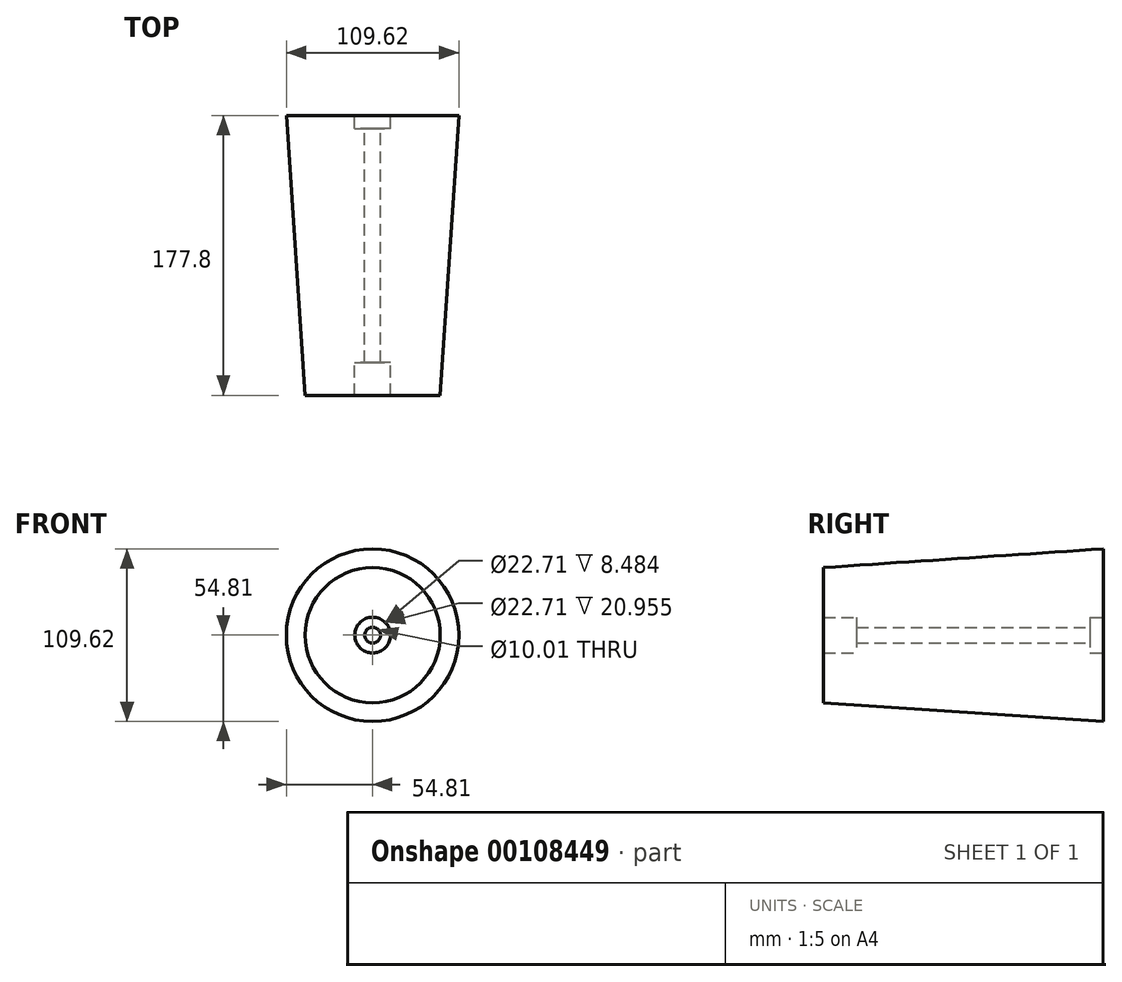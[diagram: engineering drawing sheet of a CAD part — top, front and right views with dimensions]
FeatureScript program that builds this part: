
annotation { "Feature Type Name" : "Feature", "Feature Type Description" : "" }
export const myFeature = defineFeature(function(context is Context, id is Id, definition is map)
    precondition{}
    {
        {
            var Q0;
            Q0=qCreatedBy(makeId("Top.planeOp"),FACE);
            var sketch = newSketch(context, id + "F0", { "sketchPlane" : qUnion([Q0])});
            skLineSegment(sketch, "E0", {"start": v(0, 177.8) * mm, "end": v(0, -177.8) * mm, "construction": true});
            skLineSegment(sketch, "E1", {"start": v(-177.8, 0) * mm, "end": v(177.8, 0) * mm, "construction": true});
            skLineSegment(sketch, "E2", {"start": v(-11.35, 88.9) * mm, "end": v(-54.81, 88.9) * mm});
            skLineSegment(sketch, "E3", {"start": v(-54.81, 88.9) * mm, "end": v(-42.93, -88.9) * mm});
            skLineSegment(sketch, "E4", {"start": v(-42.93, -88.9) * mm, "end": v(-11.35, -88.9) * mm});
            skLineSegment(sketch, "E5", {"start": v(-11.35, 88.9) * mm, "end": v(-11.35, 80.42) * mm});
            skLineSegment(sketch, "E6", {"start": v(-11.35, 80.42) * mm, "end": v(-5, 80.42) * mm});
            skLineSegment(sketch, "E7", {"start": v(-5, 80.42) * mm, "end": v(-5, -67.95) * mm});
            skLineSegment(sketch, "E8", {"start": v(-5, -67.95) * mm, "end": v(-11.35, -67.95) * mm});
            skLineSegment(sketch, "E9", {"start": v(-11.35, -67.95) * mm, "end": v(-11.35, -88.9) * mm});
            skPoint(sketch, "E10.orphan", {"position": v(0, 88.9) * mm});
            skPoint(sketch, "E11.orphan", {"position": v(0, -88.9) * mm});
            skSolve(sketch);
        }
        {
            var Q0;
            Q0=makeQuery(id+"F0.imprint","IMPRINT",FACE,{"disambiguationData":[TD([[makeQuery(id+"F0.imprint","IMPRINT",EDGE,{"derivedFrom":sQuery(id+"F0.wireOp",EDGE,"E2")}),1.0]])]});
            var Q1;
            Q1=sQuery(id+"F0.wireOp",EDGE,"E0");
            revolve(context, id + "F1", {"entities" : qUnion([Q0]), "axis" : qUnion([Q1]), "revolveType" : RevolveType.FULL});
        }
    });
